# Revit family: LIANO II HAND SHWR 3S
name_source: partatom
category: Plumbing Fixtures
units: mm (PartAtom-declared; Revit-internal decimal feet)

## family parameters
Cut with Voids When Loaded = No
Host = Face
OmniClass Number = 23.45.05.14.17
OmniClass Title = Showers
Part Type = Normal
Room Calculation Point = No
Round Connector Dimension = Use Diameter
Shared = No

## types (6) — shared parameters
Assembly Code = D2020300
CW Connection = Yes
HW Connection = Yes
Manufacturer = GWA Bathrooms & Kitchens
Material_Sprays = GWA-Plastic-General
URL = https://www.caroma.com.au
Vent Connection = No
Waste Connection = No
zero-valued in all types: Default Elevation

## per-type parameters (varying)
| type | Material | Model |
| LIANO II HAND SHWR 3S CHROME | GWA_Metal-Chrome | 96474C3A |
| LIANO II HAND SHWR 3S BBRASS | GWA_Metal-Brushed-Brass | 96474BB3A |
| LIANO II HAND SHWR 3S BLACK | GWA-Metal-Black | 96474B3A |
| LIANO II HAND SHWR 3S GUNMETAL | GWA_Metal-Brushed-Gunmetal | 96474GM3A |
| LIANO II HAND SHWR 3S BNICKEL | GWA_Metal-Brushed-Nickel | 96474BN3A |
| LIANO II HAND SHWR 3S BBRONZE | GWA_Metal-Brushed-Bronze | 96474BBZ3A |

note: column(s) folded — value = type name in every type: Description

## geometry (parser evidence)
native form markers: Sweep x6
no freeform markers — native parametric forms only
